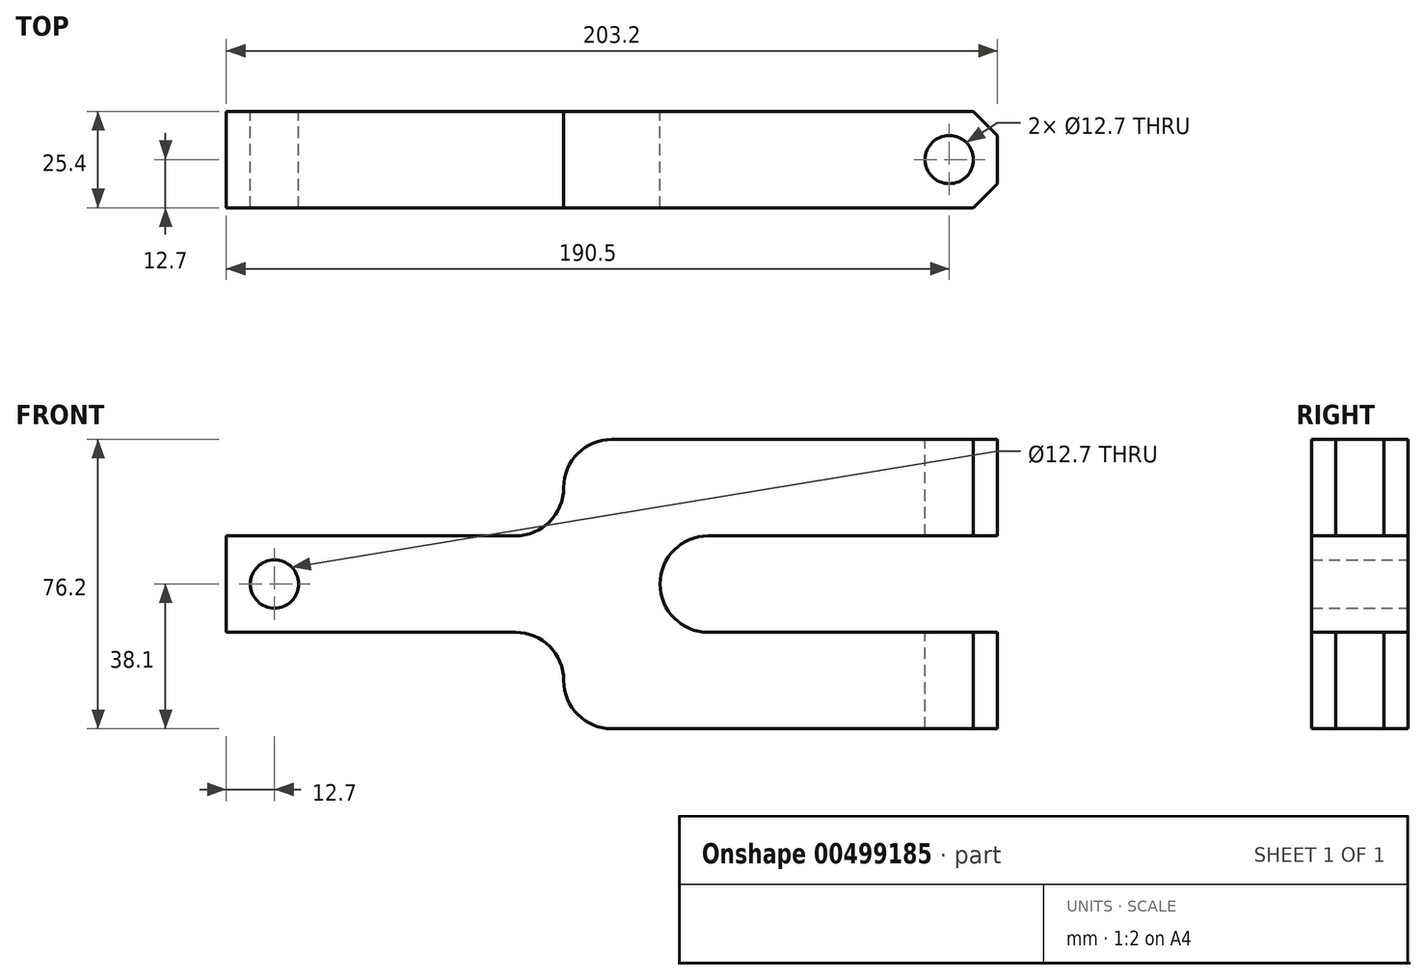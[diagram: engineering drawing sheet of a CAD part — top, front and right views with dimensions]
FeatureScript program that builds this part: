
annotation { "Feature Type Name" : "Feature", "Feature Type Description" : "" }
export const myFeature = defineFeature(function(context is Context, id is Id, definition is map)
    precondition{}
    {
        {
            var Q0;
            Q0=qCreatedBy(makeId("Front.planeOp"),FACE);
            var sketch = newSketch(context, id + "F0", { "sketchPlane" : qUnion([Q0])});
            skLineSegment(sketch, "E0", {"start": v(0, 0) * mm, "end": v(76.2, 0) * mm});
            skLineSegment(sketch, "E1", {"start": v(76.2, 25.4) * mm, "end": v(0, 25.4) * mm});
            skLineSegment(sketch, "E2", {"start": v(0, 25.4) * mm, "end": v(0, 0) * mm});
            skLineSegment(sketch, "E3", {"start": v(88.9, 38.1) * mm, "end": v(88.9, 38.1) * mm});
            skLineSegment(sketch, "E4", {"start": v(203.2, 50.8) * mm, "end": v(203.2, 25.4) * mm});
            skLineSegment(sketch, "E5", {"start": v(203.2, 25.4) * mm, "end": v(127, 25.4) * mm});
            skLineSegment(sketch, "E6", {"start": v(127, 0) * mm, "end": v(203.2, 0) * mm});
            skLineSegment(sketch, "E7", {"start": v(101.6, 50.8) * mm, "end": v(203.2, 50.8) * mm});
            skLineSegment(sketch, "E8", {"start": v(88.9, -12.7) * mm, "end": v(88.9, -12.7) * mm});
            skLineSegment(sketch, "E9", {"start": v(101.6, -25.4) * mm, "end": v(203.2, -25.4) * mm});
            skLineSegment(sketch, "E10", {"start": v(203.2, -25.4) * mm, "end": v(203.2, 0) * mm});
            skCircle(sketch, "E11", {"center": v(12.7, 12.7) * mm, "radius": 6.35 * mm});
            skPoint(sketch, "E12.visualSharp", {"position": v(107.95, 25.4) * mm});
            skArc(sketch, "E12.filletArc", {"start": v(127, 25.4) * mm, "mid": v(118.02, 21.68) * mm, "end": v(114.3, 12.7) * mm});
            skPoint(sketch, "E13.visualSharp", {"position": v(107.95, 0) * mm});
            skArc(sketch, "E13.filletArc", {"start": v(114.3, 12.7) * mm, "mid": v(118.02, 3.72) * mm, "end": v(127, 0) * mm});
            skPoint(sketch, "E14.visualSharp", {"position": v(88.9, 0) * mm});
            skArc(sketch, "E14.filletArc", {"start": v(88.9, -12.7) * mm, "mid": v(85.18, -3.72) * mm, "end": v(76.2, 0) * mm});
            skPoint(sketch, "E15.visualSharp", {"position": v(88.9, 25.4) * mm});
            skArc(sketch, "E15.filletArc", {"start": v(76.2, 25.4) * mm, "mid": v(85.18, 29.12) * mm, "end": v(88.9, 38.1) * mm});
            skPoint(sketch, "E16.visualSharp", {"position": v(88.9, -25.4) * mm});
            skArc(sketch, "E16.filletArc", {"start": v(88.9, -12.7) * mm, "mid": v(92.62, -21.68) * mm, "end": v(101.6, -25.4) * mm});
            skPoint(sketch, "E17.visualSharp", {"position": v(88.9, 50.8) * mm});
            skArc(sketch, "E17.filletArc", {"start": v(101.6, 50.8) * mm, "mid": v(92.62, 47.08) * mm, "end": v(88.9, 38.1) * mm});
            skLineSegment(sketch, "E18", {"start": v(114.3, 12.7) * mm, "end": v(114.3, 12.7) * mm});
            skSolve(sketch);
        }
        {
            var Q0;
            Q0=qCreatedBy(makeId("Top.planeOp"),FACE);
            var sketch = newSketch(context, id + "F1", { "sketchPlane" : qUnion([Q0])});
            skCircle(sketch, "E19", {"center": v(190.5, -12.7) * mm, "radius": 6.35 * mm});
            skSolve(sketch);
        }
        {
            var Q0;
            Q0 = qSketchRegion(id + "F0", true);
            extrude(context, id + "F2", {"entities" : qUnion([Q0]), "depth" : 25.4 * mm, "offsetDistance" : 25.4 * mm});
        }
        {
            var Q0;
            Q0=makeQuery(id+"F2.opExtrude","CAP_EDGE",EDGE,{"disambiguationData":[OSD([sQuery(id+"F0.wireOp",EDGE,"E4")])],"isStart":false});
            var Q1;
            Q1=makeQuery(id+"F2.opExtrude","CAP_EDGE",EDGE,{"disambiguationData":[OSD([sQuery(id+"F0.wireOp",EDGE,"E10")])],"isStart":false});
            var Q2;
            Q2=makeQuery(id+"F2.opExtrude","CAP_EDGE",EDGE,{"disambiguationData":[OSD([sQuery(id+"F0.wireOp",EDGE,"E10")])],"isStart":true});
            var Q3;
            Q3=makeQuery(id+"F2.opExtrude","CAP_EDGE",EDGE,{"disambiguationData":[OSD([sQuery(id+"F0.wireOp",EDGE,"E4")])],"isStart":true});
            chamfer(context, id + "F3", {"entities" : qUnion([Q0, Q1, Q2, Q3]), "chamferType" : ChamferType.OFFSET_ANGLE, "width" : 6.35 * mm, "oppositeDirection" : false, "angle" : 45 * degree, "tangentPropagation" : true});
        }
        {
            var Q0;
            Q0 = qSketchRegion(id + "F1", true);
            extrude(context, id + "F4", {"entities" : qUnion([Q0]), "operationType" : NewBodyOperationType.REMOVE, "endBound" : BoundingType.SYMMETRIC, "oppositeDirection" : true, "depth" : 254 * mm, "offsetDistance" : 25.4 * mm});
        }
    });
